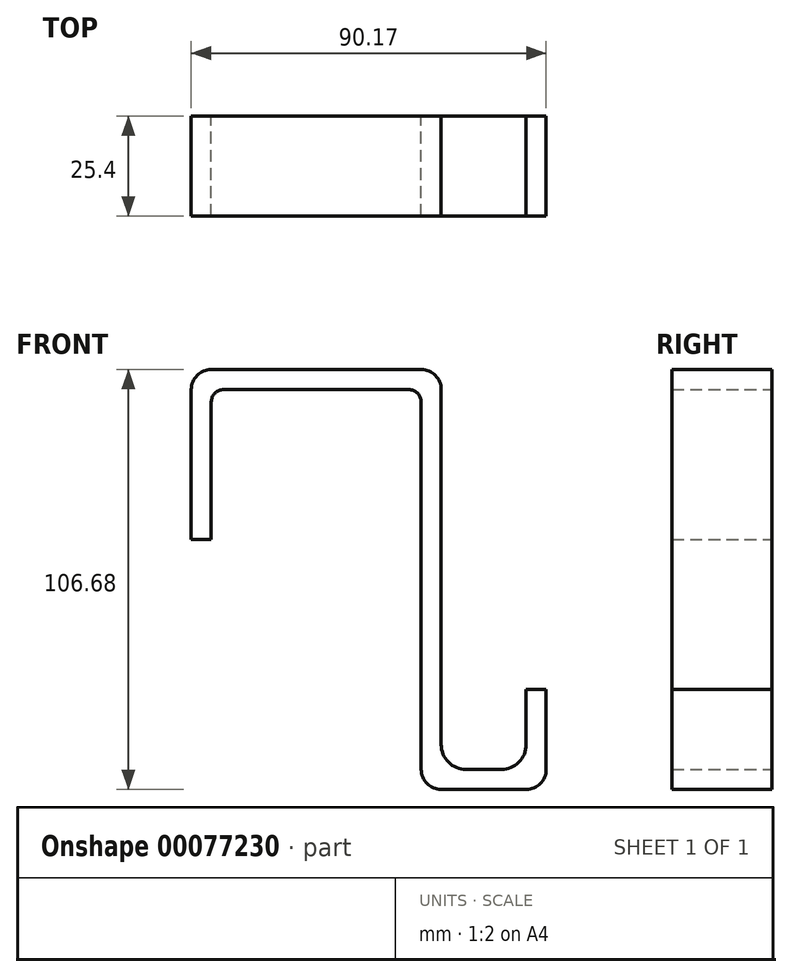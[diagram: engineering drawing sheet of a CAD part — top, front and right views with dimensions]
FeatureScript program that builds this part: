
annotation { "Feature Type Name" : "Feature", "Feature Type Description" : "" }
export const myFeature = defineFeature(function(context is Context, id is Id, definition is map)
    precondition{}
    {
        {
            var Q0;
            Q0=qCreatedBy(makeId("Front.planeOp"),FACE);
            var sketch = newSketch(context, id + "F0", { "sketchPlane" : qUnion([Q0])});
            skLineSegment(sketch, "E0", {"start": v(0, 0) * mm, "end": v(0, 43.18) * mm});
            skLineSegment(sketch, "E1", {"start": v(0, 43.18) * mm, "end": v(63.5, 43.18) * mm});
            skLineSegment(sketch, "E2", {"start": v(63.5, 43.18) * mm, "end": v(63.5, -52.07) * mm});
            skLineSegment(sketch, "E3", {"start": v(69.85, -58.42) * mm, "end": v(78.74, -58.42) * mm});
            skLineSegment(sketch, "E4", {"start": v(85.1, -52.07) * mm, "end": v(85.1, -38.1) * mm});
            skLineSegment(sketch, "E5.0", {"start": v(90.17, -63.5) * mm, "end": v(90.17, -38.1) * mm});
            skLineSegment(sketch, "E5.1", {"start": v(5.08, 0) * mm, "end": v(5.08, 34.93) * mm});
            skLineSegment(sketch, "E5.2", {"start": v(8.25, 38.1) * mm, "end": v(55.25, 38.1) * mm});
            skLineSegment(sketch, "E5.3", {"start": v(58.42, 34.93) * mm, "end": v(58.42, -63.5) * mm});
            skLineSegment(sketch, "E5.4", {"start": v(58.42, -63.5) * mm, "end": v(90.17, -63.5) * mm});
            skLineSegment(sketch, "E6", {"start": v(5.08, 0) * mm, "end": v(0, 0) * mm});
            skLineSegment(sketch, "E7", {"start": v(85.1, -38.1) * mm, "end": v(90.17, -38.1) * mm});
            skPoint(sketch, "E8.visualSharp", {"position": v(63.5, -58.42) * mm});
            skArc(sketch, "E8.filletArc", {"start": v(63.5, -52.07) * mm, "mid": v(65.36, -56.56) * mm, "end": v(69.85, -58.42) * mm});
            skPoint(sketch, "E9.visualSharp", {"position": v(85.1, -58.42) * mm});
            skArc(sketch, "E9.filletArc", {"start": v(78.74, -58.42) * mm, "mid": v(83.23, -56.56) * mm, "end": v(85.1, -52.07) * mm});
            skPoint(sketch, "E10.visualSharp", {"position": v(5.08, 38.1) * mm});
            skPoint(sketch, "E11.visualSharp", {"position": v(58.42, 38.1) * mm});
            skArc(sketch, "E12.filletArc", {"start": v(8.25, 38.1) * mm, "mid": v(6, 37.17) * mm, "end": v(5.08, 34.93) * mm});
            skArc(sketch, "E13.filletArc", {"start": v(58.42, 34.93) * mm, "mid": v(57.5, 37.17) * mm, "end": v(55.25, 38.1) * mm});
            skSolve(sketch);
        }
        {
            var Q0;
            Q0 = qSketchRegion(id + "F0", true);
            extrude(context, id + "F1", {"entities" : qUnion([Q0]), "depth" : 25.4 * mm});
        }
        {
            var Q0;
            Q0=makeQuery(id+"F1.opExtrude","SWEPT_EDGE",EDGE,{"disambiguationData":[OSD([sQuery(id+"F0.wireOp",EDGE,"E0"),sQuery(id+"F0.wireOp",EDGE,"E1")])]});
            var Q1;
            Q1=makeQuery(id+"F1.opExtrude","SWEPT_EDGE",EDGE,{"disambiguationData":[OSD([sQuery(id+"F0.wireOp",EDGE,"E1"),sQuery(id+"F0.wireOp",EDGE,"E2")])]});
            var Q2;
            Q2=makeQuery(id+"F1.opExtrude","SWEPT_EDGE",EDGE,{"disambiguationData":[OSD([sQuery(id+"F0.wireOp",EDGE,"E5.0"),sQuery(id+"F0.wireOp",EDGE,"E5.4")])]});
            var Q3;
            Q3=makeQuery(id+"F1.opExtrude","SWEPT_EDGE",EDGE,{"disambiguationData":[OSD([sQuery(id+"F0.wireOp",EDGE,"E5.3"),sQuery(id+"F0.wireOp",EDGE,"E5.4")])]});
            fillet(context, id + "F2", {"entities" : qUnion([Q0, Q1, Q2, Q3]), "radius" : 5.08 * mm, "tangentPropagation" : true, "allowEdgeOverflow" : false});
        }
    });
